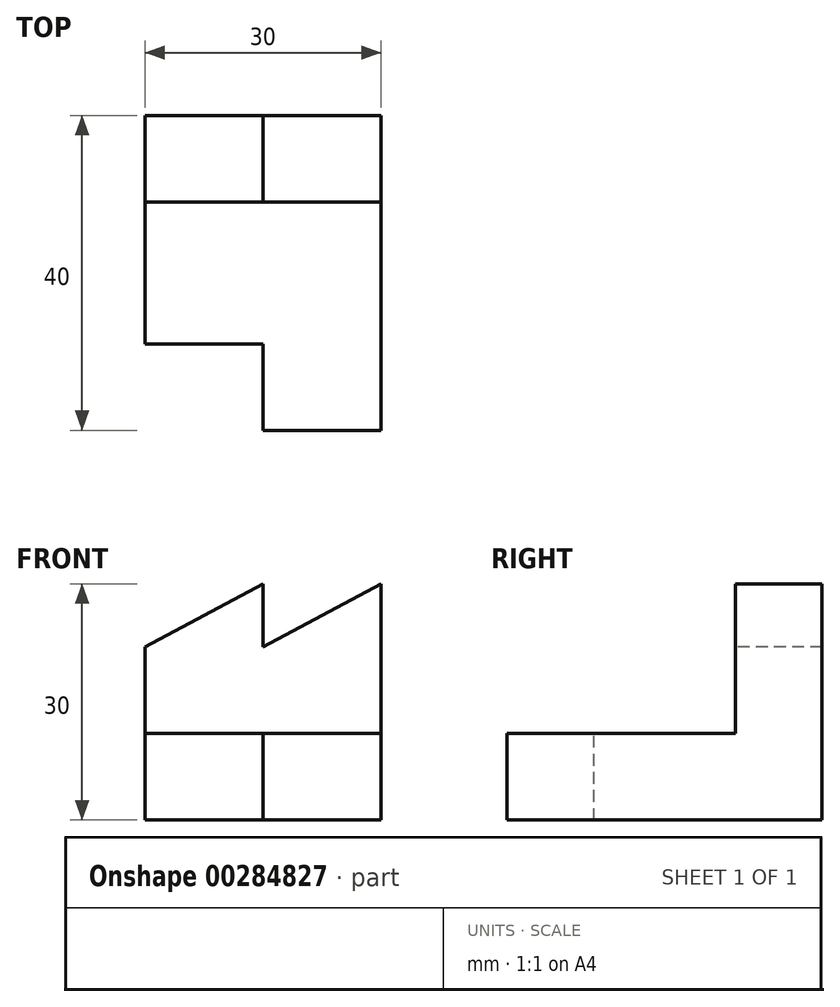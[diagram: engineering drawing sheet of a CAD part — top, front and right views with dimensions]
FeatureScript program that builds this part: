
annotation { "Feature Type Name" : "Feature", "Feature Type Description" : "" }
export const myFeature = defineFeature(function(context is Context, id is Id, definition is map)
    precondition{}
    {
        {
            var Q0;
            Q0=qCreatedBy(makeId("Front.planeOp"),FACE);
            var sketch = newSketch(context, id + "F0", { "sketchPlane" : qUnion([Q0])});
            skLineSegment(sketch, "E0.bottom", {"start": v(0, 0) * mm, "end": v(40, 0) * mm});
            skLineSegment(sketch, "E0.top", {"start": v(0, 30) * mm, "end": v(40, 30) * mm});
            skLineSegment(sketch, "E0.left", {"start": v(0, 0) * mm, "end": v(0, 30) * mm});
            skLineSegment(sketch, "E0.right", {"start": v(40, 0) * mm, "end": v(40, 30) * mm});
            skLineSegment(sketch, "E1.bottom", {"start": v(40, 30) * mm, "end": v(11, 30) * mm});
            skLineSegment(sketch, "E1.top", {"start": v(40, 11) * mm, "end": v(11, 11) * mm});
            skLineSegment(sketch, "E1.left", {"start": v(40, 30) * mm, "end": v(40, 11) * mm});
            skLineSegment(sketch, "E1.right", {"start": v(11, 30) * mm, "end": v(11, 11) * mm});
            skSolve(sketch);
        }
        {
            var Q0;
            Q0=makeQuery(id+"F0.imprint","IMPRINT",FACE,{"disambiguationData":[TD([[makeQuery(id+"F0.imprint","IMPRINT",EDGE,{"derivedFrom":sQuery(id+"F0.wireOp",EDGE,"E0.bottom")}),1.0]])]});
            extrude(context, id + "F1", {"entities" : qUnion([Q0]), "depth" : 30 * mm});
        }
        {
            var Q0;
            Q0=makeQuery(id+"F1.opExtrude","SWEPT_FACE",FACE,{"disambiguationData":[OSD([sQuery(id+"F0.wireOp",EDGE,"E1.top")])]});
            var sketch = newSketch(context, id + "F2", { "sketchPlane" : qUnion([Q0])});
            skPoint(sketch, "E2.oppositeSnap0", {"position": v(40, -15) * mm});
            skLineSegment(sketch, "E2.bottom", {"start": v(40, -30) * mm, "end": v(29, -30) * mm});
            skLineSegment(sketch, "E2.top", {"start": v(40, -15) * mm, "end": v(29, -15) * mm});
            skLineSegment(sketch, "E2.left", {"start": v(40, -30) * mm, "end": v(40, -15) * mm});
            skLineSegment(sketch, "E2.right", {"start": v(29, -30) * mm, "end": v(29, -15) * mm});
            skSolve(sketch);
        }
        {
            var Q0;
            Q0=qSketchRegion(id+"F2",true);
            var Q1;
            Q1=makeQuery(id+"F1.opExtrude","CAP_VERTEX",VERTEX,{"disambiguationData":[OSD([sQuery(id+"F0.wireOp",EDGE,"E0.bottom"),sQuery(id+"F0.wireOp",EDGE,"E0.right")])],"isStart":false});
            extrude(context, id + "F3", {"entities" : qUnion([Q0]), "operationType" : NewBodyOperationType.REMOVE, "endBound" : BoundingType.UP_TO_VERTEX, "oppositeDirection" : true, "endBoundEntityVertex" : qUnion([Q1]), "depth" : 25 * mm});
        }
        {
            var Q0;
            Q0=makeQuery(id+"F1.opExtrude","SWEPT_FACE",FACE,{"disambiguationData":[OSD([sQuery(id+"F0.wireOp",EDGE,"E1.right")])]});
            var sketch = newSketch(context, id + "F4", { "sketchPlane" : qUnion([Q0])});
            skPoint(sketch, "E3.oppositeSnap0", {"position": v(-15, 30) * mm});
            skLineSegment(sketch, "E3.bottom", {"start": v(-30, 30) * mm, "end": v(-15, 30) * mm});
            skLineSegment(sketch, "E3.top", {"start": v(-30, 22) * mm, "end": v(-15, 22) * mm});
            skLineSegment(sketch, "E3.left", {"start": v(-30, 30) * mm, "end": v(-30, 22) * mm});
            skLineSegment(sketch, "E3.right", {"start": v(-15, 30) * mm, "end": v(-15, 22) * mm});
            skSolve(sketch);
        }
        {
            var Q0;
            Q0=qSketchRegion(id+"F4",true);
            var Q1;
            Q1=makeQuery(id+"F1.opExtrude","CAP_VERTEX",VERTEX,{"disambiguationData":[OSD([sQuery(id+"F0.wireOp",EDGE,"E0.top"),sQuery(id+"F0.wireOp",EDGE,"E0.left")])],"isStart":false});
            extrude(context, id + "F5", {"entities" : qUnion([Q0]), "operationType" : NewBodyOperationType.REMOVE, "endBound" : BoundingType.UP_TO_VERTEX, "oppositeDirection" : true, "endBoundEntityVertex" : qUnion([Q1]), "depth" : 25 * mm});
        }
        {
            var Q0;
            Q0=makeQuery(id+"F1.opExtrude","SWEPT_BODY",BODY,{"disambiguationData":[OSD([sQuery(id+"F0.wireOp",EDGE,"E0.bottom"),sQuery(id+"F0.wireOp",EDGE,"E0.top"),sQuery(id+"F0.wireOp",EDGE,"E0.left"),sQuery(id+"F0.wireOp",EDGE,"E0.right"),sQuery(id+"F0.wireOp",EDGE,"E1.top"),sQuery(id+"F0.wireOp",EDGE,"E1.right")])]});
            var Q1;
            Q1=makeQuery(id+"F1.opExtrude","CAP_EDGE",EDGE,{"disambiguationData":[OSD([sQuery(id+"F0.wireOp",EDGE,"E0.left")])],"isStart":true});
            transform(context, id + "F6", {"entities" : qUnion([Q0]), "transformType" : TransformType.ROTATION, "transformAxis" : qUnion([Q1]), "angle" : 90 * degree, "oppositeDirection" : true, "makeCopy" : false});
        }
        {
            var Q0;
            Q0=makeQuery(id+"F1.opExtrude","SWEPT_FACE",FACE,{"disambiguationData":[OSD([sQuery(id+"F0.wireOp",EDGE,"E1.right")])]});
            var sketch = newSketch(context, id + "F7", { "sketchPlane" : qUnion([Q0])});
            skLineSegment(sketch, "E4", {"start": v(-15, 30) * mm, "end": v(-30, 22) * mm});
            skSolve(sketch);
        }
        {
            var Q0;
            Q0=makeQuery(id+"F7.imprint","IMPRINT",FACE,{"disambiguationData":[TD([[makeQuery(id+"F7.imprint","IMPRINT",EDGE,{"derivedFrom":sQuery(id+"F7.wireOp",EDGE,"E4")}),1.0]])]});
            var Q1;
            Q1=makeQuery(id+"F5.boolean.opBoolean","COPY",VERTEX,{"derivedFrom":makeQuery(id+"F5.opExtrude","CAP_VERTEX",VERTEX,{"disambiguationData":[OSD([sQuery(id+"F0.wireOp",EDGE,"E0.top"),sQuery(id+"F0.wireOp",EDGE,"E1.bottom"),sQuery(id+"F0.wireOp",EDGE,"E1.right"),sQuery(id+"F4.wireOp",EDGE,"E3.bottom"),sQuery(id+"F4.wireOp",EDGE,"E3.right"),dummyQuery(id+"F5.vertexPlane.planeOp",FACE)])],"isStart":false})});
            extrude(context, id + "F8", {"entities" : qUnion([Q0]), "operationType" : NewBodyOperationType.ADD, "endBound" : BoundingType.UP_TO_VERTEX, "oppositeDirection" : true, "endBoundEntityVertex" : qUnion([Q1]), "depth" : 25 * mm});
        }
        {
            var Q0;
            Q0=makeQuery(id+"F8.boolean.opBoolean","MERGE",FACE,{"derivedFrom":[makeQuery(id+"F1.opExtrude","SWEPT_FACE",FACE,{"disambiguationData":[OSD([sQuery(id+"F0.wireOp",EDGE,"E1.right")])]}),makeQuery(id+"F8.opExtrude","CAP_FACE",FACE,{"disambiguationData":[OSD([sQuery(id+"F4.wireOp",EDGE,"E3.top"),sQuery(id+"F4.wireOp",EDGE,"E3.right"),sQuery(id+"F7.wireOp",EDGE,"E4")])],"isStart":true})]});
            var sketch = newSketch(context, id + "F9", { "sketchPlane" : qUnion([Q0])});
            skLineSegment(sketch, "E5", {"start": v(-15, 30) * mm, "end": v(-15, 22) * mm});
            skLineSegment(sketch, "E6", {"start": v(-15, 22) * mm, "end": v(0, 30) * mm});
            skSolve(sketch);
        }
        {
            var Q0;
            Q0=makeQuery(id+"F9.imprint","IMPRINT",FACE,{"disambiguationData":[TD([[makeQuery(id+"F9.imprint","IMPRINT",EDGE,{"derivedFrom":sQuery(id+"F9.wireOp",EDGE,"E5")}),1.0]])]});
            var Q1;
            {var subQ0=sQuery(id+"F4.wireOp",EDGE,"E3.right");var subQ1=sQuery(id+"F0.wireOp",EDGE,"E1.right");var subQ2=sQuery(id+"F0.wireOp",EDGE,"E1.bottom");var subQ3=sQuery(id+"F0.wireOp",EDGE,"E0.top");Q1=makeQuery(id+"F8.boolean.opBoolean","MERGE",VERTEX,{"derivedFrom":[makeQuery(id+"F5.boolean.opBoolean","COPY",VERTEX,{"derivedFrom":makeQuery(id+"F5.opExtrude","CAP_VERTEX",VERTEX,{"disambiguationData":[OSD([subQ3,subQ2,subQ1,sQuery(id+"F4.wireOp",EDGE,"E3.bottom"),subQ0,dummyQuery(id+"F5.vertexPlane.planeOp",FACE)])],"isStart":false})}),makeQuery(id+"F8.opExtrude","CAP_VERTEX",VERTEX,{"disambiguationData":[OSD([subQ3,subQ2,subQ1,subQ0,sQuery(id+"F7.wireOp",EDGE,"E4"),dummyQuery(id+"F8.vertexPlane.planeOp",FACE)])],"isStart":false})]});}
            extrude(context, id + "F10", {"entities" : qUnion([Q0]), "operationType" : NewBodyOperationType.REMOVE, "endBound" : BoundingType.UP_TO_VERTEX, "oppositeDirection" : true, "endBoundEntityVertex" : qUnion([Q1]), "depth" : 25 * mm});
        }
    });
